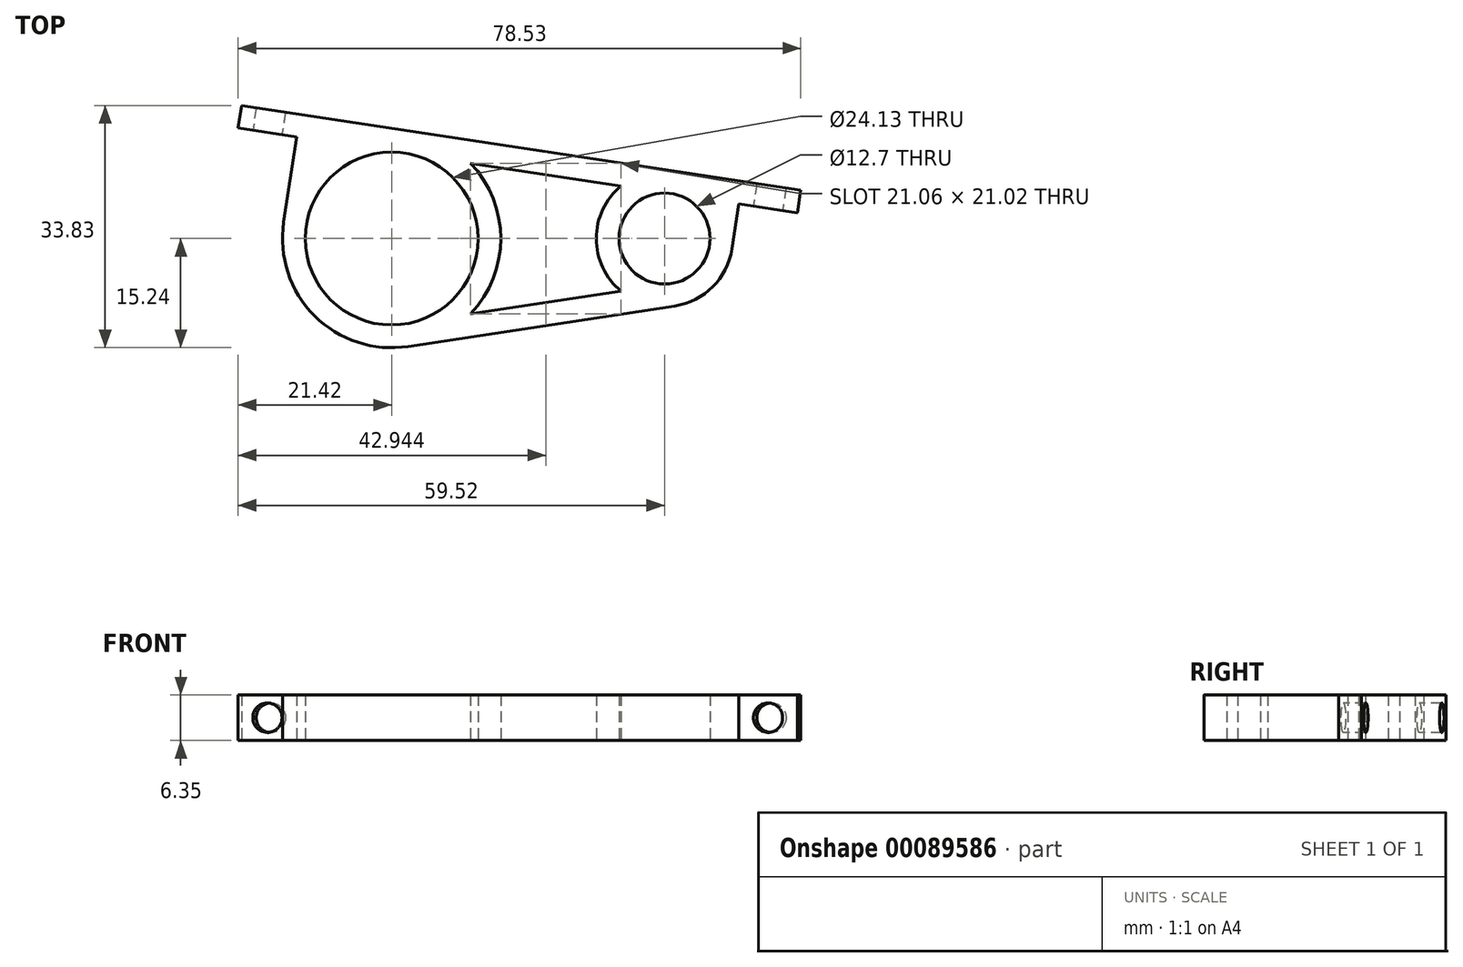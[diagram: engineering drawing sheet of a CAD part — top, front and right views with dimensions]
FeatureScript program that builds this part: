
annotation { "Feature Type Name" : "Feature", "Feature Type Description" : "" }
export const myFeature = defineFeature(function(context is Context, id is Id, definition is map)
    precondition{}
    {
        {
            var Q0;
            Q0=qCreatedBy(makeId("Top.planeOp"),FACE);
            var sketch = newSketch(context, id + "F0", { "sketchPlane" : qUnion([Q0])});
            skCircle(sketch, "E0", {"center": v(0, 0) * mm, "radius": 6.35 * mm});
            skCircle(sketch, "E1", {"center": v(-38.1, 0) * mm, "radius": 12.07 * mm});
            skLineSegment(sketch, "E2", {"start": v(-36.3, 11.93) * mm, "end": v(0.95, 6.28) * mm, "construction": true});
            skLineSegment(sketch, "E3", {"start": v(-50.88, 17.35) * mm, "end": v(10.85, 7.99) * mm});
            skLineSegment(sketch, "E4", {"start": v(10.85, 7.99) * mm, "end": v(9.42, -1.43) * mm});
            skLineSegment(sketch, "E5", {"start": v(1.43, -9.42) * mm, "end": v(-35.81, -15.07) * mm});
            skLineSegment(sketch, "E6", {"start": v(-53.17, 2.29) * mm, "end": v(-50.88, 17.35) * mm});
            skLineSegment(sketch, "E7", {"start": v(9.42, -1.43) * mm, "end": v(6.28, -0.95) * mm, "construction": true});
            skLineSegment(sketch, "E8", {"start": v(6.28, -0.95) * mm, "end": v(7.03, 3.99) * mm, "construction": true});
            skLineSegment(sketch, "E9", {"start": v(1.43, -9.42) * mm, "end": v(0.95, -6.28) * mm, "construction": true});
            skLineSegment(sketch, "E10", {"start": v(0.95, -6.28) * mm, "end": v(2.8, -6) * mm, "construction": true});
            skLineSegment(sketch, "E11", {"start": v(-53.17, 2.29) * mm, "end": v(-50.03, 1.8) * mm, "construction": true});
            skLineSegment(sketch, "E12", {"start": v(-50.03, 1.8) * mm, "end": v(-50.69, -2.53) * mm, "construction": true});
            skLineSegment(sketch, "E13", {"start": v(-36.3, -11.93) * mm, "end": v(0.95, -6.28) * mm, "construction": true});
            skLineSegment(sketch, "E14", {"start": v(-59.04, 18.6) * mm, "end": v(-59.52, 15.45) * mm});
            skLineSegment(sketch, "E15", {"start": v(-59.52, 15.45) * mm, "end": v(-51.36, 14.21) * mm});
            skLineSegment(sketch, "E16", {"start": v(-59.04, 18.6) * mm, "end": v(-50.88, 17.35) * mm});
            skLineSegment(sketch, "E17", {"start": v(10.85, 7.99) * mm, "end": v(19, 6.75) * mm});
            skLineSegment(sketch, "E18", {"start": v(19, 6.75) * mm, "end": v(18.53, 3.61) * mm});
            skLineSegment(sketch, "E19", {"start": v(18.53, 3.61) * mm, "end": v(10.37, 4.85) * mm});
            skLineSegment(sketch, "E20", {"start": v(-36.3, -11.93) * mm, "end": v(-35.81, -15.07) * mm, "construction": true});
            skArc(sketch, "E21.trimOffspring", {"start": v(-53.17, 2.29) * mm, "mid": v(-48.88, -10.78) * mm, "end": v(-35.81, -15.07) * mm});
            skArc(sketch, "E22", {"start": v(1.43, -9.42) * mm, "mid": v(6.74, -6.74) * mm, "end": v(9.42, -1.43) * mm});
            skArc(sketch, "E23", {"start": v(-35.81, 15.07) * mm, "mid": v(-53.34, 0) * mm, "end": v(-35.81, -15.07) * mm});
            skArc(sketch, "E24.trimOffspring", {"start": v(-6.07, 7.34) * mm, "mid": v(-9.53, 0) * mm, "end": v(-6.07, -7.34) * mm});
            skLineSegment(sketch, "E25", {"start": v(-27.08, -10.53) * mm, "end": v(-6.07, -7.34) * mm});
            skArc(sketch, "E26.trimOffspring", {"start": v(-27.08, -10.53) * mm, "mid": v(-22.86, 0) * mm, "end": v(-27.08, 10.53) * mm});
            skLineSegment(sketch, "E27", {"start": v(-27.08, 10.53) * mm, "end": v(-6.07, 7.34) * mm});
            skLineSegment(sketch, "E28", {"start": v(-54.96, 17.97) * mm, "end": v(-55.44, 14.83) * mm, "construction": true});
            skLineSegment(sketch, "E29", {"start": v(14.93, 7.37) * mm, "end": v(14.45, 4.23) * mm, "construction": true});
            skSolve(sketch);
        }
        {
            var Q0;
            Q0=qSketchRegion(id+"F0",true);
            extrude(context, id + "F1", {"entities" : qUnion([Q0]), "depth" : 6.35 * mm});
        }
        {
            var Q0;
            Q0=makeQuery(id+"F1.opExtrude","SWEPT_FACE",FACE,{"disambiguationData":[OSD([sQuery(id+"F0.wireOp",EDGE,"E15")])]});
            var sketch = newSketch(context, id + "F2", { "sketchPlane" : qUnion([Q0])});
            skLineSegment(sketch, "E30", {"start": v(-57.04, 6.35) * mm, "end": v(-57.04, 0) * mm, "construction": true});
            skCircle(sketch, "E31", {"center": v(-57.04, 3.18) * mm, "radius": 2.06 * mm});
            skSolve(sketch);
        }
        {
            var Q0;
            Q0=qSketchRegion(id+"F2",true);
            extrude(context, id + "F3", {"entities" : qUnion([Q0]), "operationType" : NewBodyOperationType.REMOVE, "endBound" : BoundingType.THROUGH_ALL, "oppositeDirection" : true, "depth" : 25.4 * mm});
        }
        {
            var Q0;
            Q0=makeQuery(id+"F1.opExtrude","SWEPT_FACE",FACE,{"disambiguationData":[OSD([sQuery(id+"F0.wireOp",EDGE,"E19")])]});
            var sketch = newSketch(context, id + "F4", { "sketchPlane" : qUnion([Q0])});
            skLineSegment(sketch, "E32", {"start": v(13.65, 6.35) * mm, "end": v(13.65, 0) * mm, "construction": true});
            skCircle(sketch, "E33", {"center": v(13.65, 3.18) * mm, "radius": 2.06 * mm});
            skSolve(sketch);
        }
        {
            var Q0;
            Q0=makeQuery(id+"F4.imprint","IMPRINT",FACE,{"disambiguationData":[TD([[makeQuery(id+"F4.imprint","IMPRINT",EDGE,{"derivedFrom":sQuery(id+"F4.wireOp",EDGE,"E33")}),1.0]])]});
            var Q1;
            Q1=sQuery(id+"F4.wireOp",EDGE,"E33");
            extrude(context, id + "F5", {"entities" : qUnion([Q0]), "operationType" : NewBodyOperationType.REMOVE, "surfaceEntities" : qUnion([Q1]), "endBound" : BoundingType.THROUGH_ALL, "oppositeDirection" : true, "depth" : 25.4 * mm});
        }
    });
